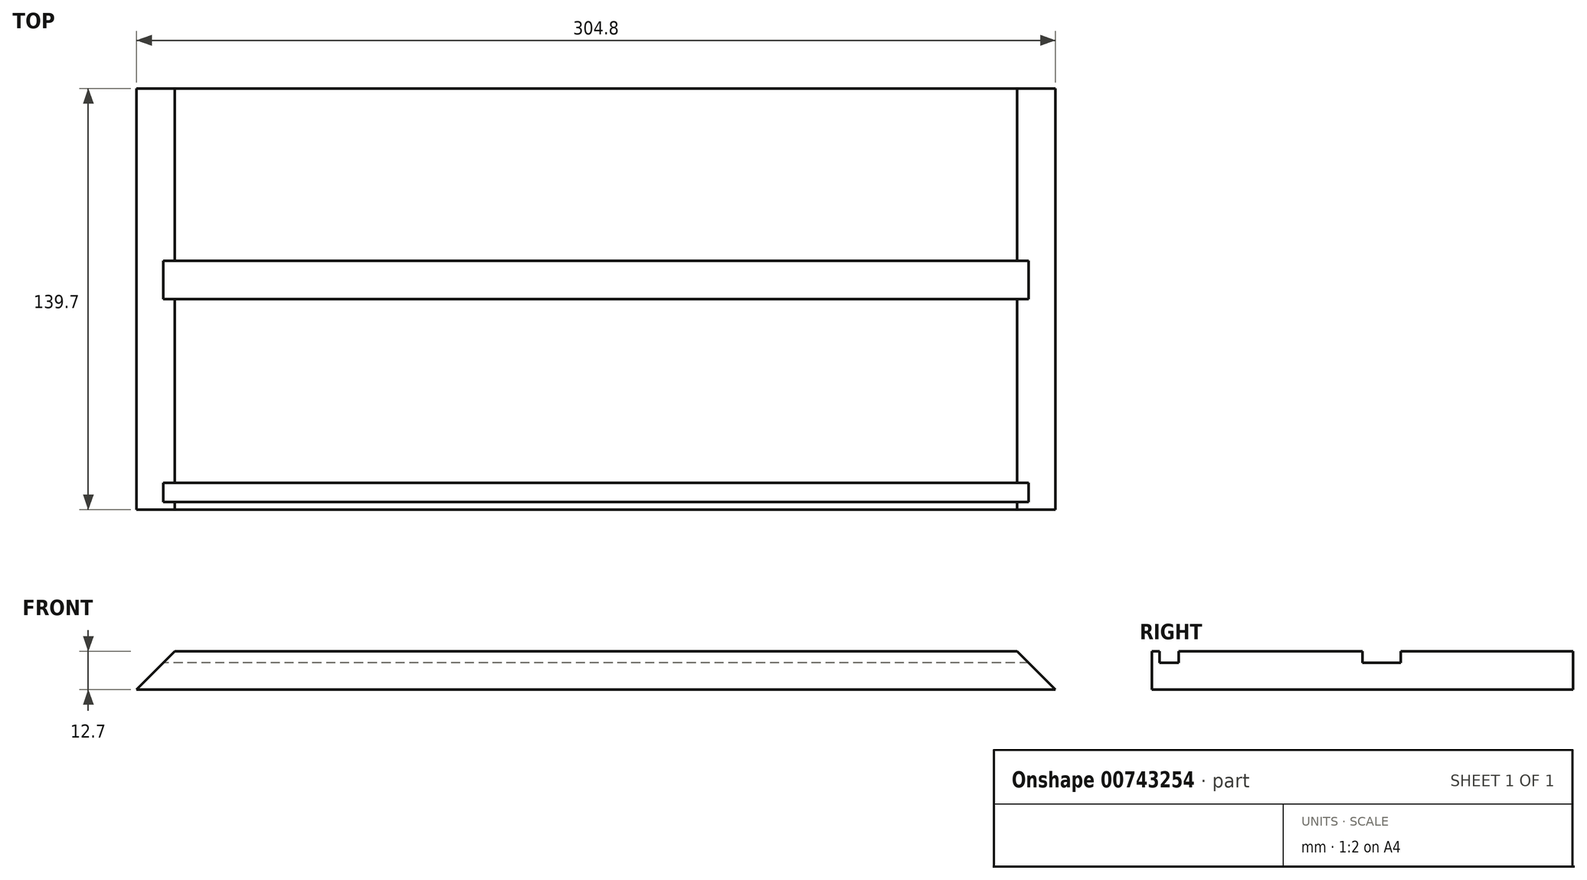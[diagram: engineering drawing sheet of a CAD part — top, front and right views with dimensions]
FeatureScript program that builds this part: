
annotation { "Feature Type Name" : "Feature", "Feature Type Description" : "" }
export const myFeature = defineFeature(function(context is Context, id is Id, definition is map)
    precondition{}
    {
        {
            var Q0;
            Q0=qCreatedBy(makeId("Top.planeOp"),FACE);
            var sketch = newSketch(context, id + "F0", { "sketchPlane" : qUnion([Q0])});
            skLineSegment(sketch, "E0.bottom", {"start": v(152.4, 63.5) * mm, "end": v(-152.4, 63.5) * mm});
            skLineSegment(sketch, "E0.top", {"start": v(152.4, -76.2) * mm, "end": v(-152.4, -76.2) * mm});
            skLineSegment(sketch, "E0.left", {"start": v(152.4, 63.5) * mm, "end": v(152.4, -76.2) * mm});
            skLineSegment(sketch, "E0.right", {"start": v(-152.4, 63.5) * mm, "end": v(-152.4, -76.2) * mm});
            skPoint(sketch, "E0.middle", {"position": v(0, 0) * mm});
            skSolve(sketch);
        }
        {
            var Q0;
            Q0=qCreatedBy(makeId("Top.planeOp"),FACE);
            cPlane(context, id + "F1", {"entities" : qUnion([Q0]), "cplaneType" : CPlaneType.OFFSET, "offset" : 12.7 * mm, "width" : 152.4 * mm, "height" : 152.4 * mm});
        }
        {
            var Q0;
            Q0=qCreatedBy(id+"F1.planeOp",FACE);
            var sketch = newSketch(context, id + "F2", { "sketchPlane" : qUnion([Q0])});
            skPoint(sketch, "E1.middle", {"position": v(0, -6.35) * mm});
            skLineSegment(sketch, "E2.bottom", {"start": v(-139.7, 63.5) * mm, "end": v(139.7, 63.5) * mm});
            skLineSegment(sketch, "E2.top", {"start": v(-139.7, -76.2) * mm, "end": v(139.7, -76.2) * mm});
            skLineSegment(sketch, "E2.left", {"start": v(-139.7, 63.5) * mm, "end": v(-139.7, -76.2) * mm});
            skLineSegment(sketch, "E2.right", {"start": v(139.7, 63.5) * mm, "end": v(139.7, -76.2) * mm});
            skSolve(sketch);
        }
        {
            var Q0;
            Q0 = qSketchRegion(id + "F0", true);
            var Q1;
            Q1 = qSketchRegion(id + "F2", true);
            loft(context, id + "F3", {"sheetProfilesArray" : [{ "sheetProfileEntities" : qUnion([Q0]) }, { "sheetProfileEntities" : qUnion([Q1]) }]});
        }
        {
            var Q0;
            Q0=qCreatedBy(id+"F1.planeOp",FACE);
            var sketch = newSketch(context, id + "F4", { "sketchPlane" : qUnion([Q0])});
            skLineSegment(sketch, "E3.bottom", {"start": v(152.4, 76.2) * mm, "end": v(-152.4, 76.2) * mm});
            skLineSegment(sketch, "E3.top", {"start": v(152.4, -76.2) * mm, "end": v(-152.4, -76.2) * mm});
            skLineSegment(sketch, "E3.left", {"start": v(152.4, 76.2) * mm, "end": v(152.4, -76.2) * mm});
            skLineSegment(sketch, "E3.right", {"start": v(-152.4, 76.2) * mm, "end": v(-152.4, -76.2) * mm});
            skPoint(sketch, "E3.middle", {"position": v(0, 0) * mm});
            skLineSegment(sketch, "E4.bottom", {"start": v(146.05, -67.31) * mm, "end": v(-146.05, -67.3) * mm});
            skLineSegment(sketch, "E4.top", {"start": v(146.05, -73.66) * mm, "end": v(-146.05, -73.66) * mm});
            skLineSegment(sketch, "E4.left", {"start": v(146.05, -67.31) * mm, "end": v(146.05, -73.66) * mm});
            skLineSegment(sketch, "E4.right", {"start": v(-146.05, -67.3) * mm, "end": v(-146.05, -73.66) * mm});
            skPoint(sketch, "E4.middle", {"position": v(0, -70.49) * mm});
            skLineSegment(sketch, "E5.bottom", {"start": v(146.05, 6.35) * mm, "end": v(-146.05, 6.35) * mm});
            skLineSegment(sketch, "E5.top", {"start": v(146.05, -6.35) * mm, "end": v(-146.05, -6.35) * mm});
            skLineSegment(sketch, "E5.left", {"start": v(146.05, 6.35) * mm, "end": v(146.05, -6.35) * mm});
            skLineSegment(sketch, "E5.right", {"start": v(-146.05, 6.35) * mm, "end": v(-146.05, -6.35) * mm});
            skSolve(sketch);
        }
        {
            var Q0;
            Q0=makeQuery(id+"F4.imprint","IMPRINT",FACE,{"disambiguationData":[TD([[makeQuery(id+"F4.imprint","IMPRINT",EDGE,{"derivedFrom":sQuery(id+"F4.wireOp",EDGE,"E4.bottom")}),1.0]])]});
            var Q1;
            Q1=makeQuery(id+"F4.imprint","IMPRINT",FACE,{"disambiguationData":[TD([[makeQuery(id+"F4.imprint","IMPRINT",EDGE,{"derivedFrom":sQuery(id+"F4.wireOp",EDGE,"E5.bottom")}),1.0]])]});
            extrude(context, id + "F5", {"entities" : qUnion([Q0, Q1]), "operationType" : NewBodyOperationType.REMOVE, "oppositeDirection" : true, "depth" : 3.8 * mm, "offsetDistance" : 25.4 * mm});
        }
    });
